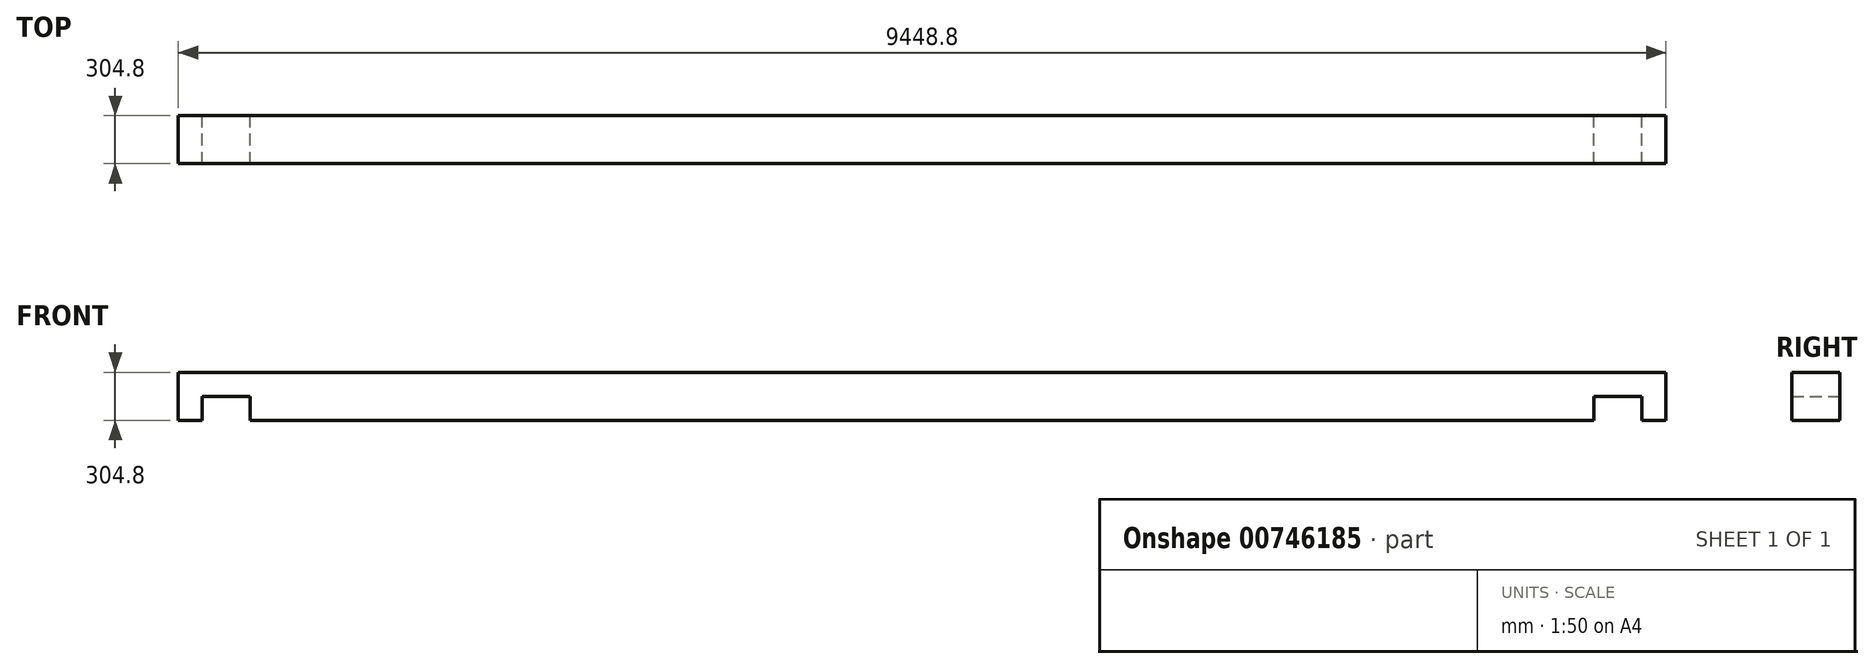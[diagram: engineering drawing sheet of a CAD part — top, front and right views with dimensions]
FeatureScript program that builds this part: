
annotation { "Feature Type Name" : "Feature", "Feature Type Description" : "" }
export const myFeature = defineFeature(function(context is Context, id is Id, definition is map)
    precondition{}
    {
        {
            var Q0;
            Q0=qCreatedBy(makeId("Front.planeOp"),FACE);
            var sketch = newSketch(context, id + "F0", { "sketchPlane" : qUnion([Q0])});
            skLineSegment(sketch, "E0", {"start": v(0, -3653.77) * mm, "end": v(0, 4269.33) * mm, "construction": true});
            skLineSegment(sketch, "E1", {"start": v(-5350.95, 0) * mm, "end": v(7707.65, 0) * mm, "construction": true});
            skLineSegment(sketch, "E2", {"start": v(0, 0) * mm, "end": v(-4267.2, 0) * mm});
            skLineSegment(sketch, "E3", {"start": v(-4267.2, 0) * mm, "end": v(-4267.2, 152.4) * mm});
            skLineSegment(sketch, "E4", {"start": v(-4267.2, 152.4) * mm, "end": v(-4572, 152.4) * mm});
            skLineSegment(sketch, "E5", {"start": v(-4572, 152.4) * mm, "end": v(-4572, 0) * mm});
            skLineSegment(sketch, "E6", {"start": v(-4572, 0) * mm, "end": v(-4724.4, 0) * mm});
            skLineSegment(sketch, "E7", {"start": v(-4724.4, 0) * mm, "end": v(-4724.4, 304.8) * mm});
            skLineSegment(sketch, "E8", {"start": v(-4724.4, 304.8) * mm, "end": v(0, 304.8) * mm});
            skLineSegment(sketch, "E9.MirrorCS", {"start": v(4267.2, 0) * mm, "end": v(4267.2, 152.4) * mm});
            skLineSegment(sketch, "E10.MirrorCS", {"start": v(4572, 0) * mm, "end": v(4724.4, 0) * mm});
            skLineSegment(sketch, "E11.MirrorCS", {"start": v(4572, 152.4) * mm, "end": v(4572, 0) * mm});
            skLineSegment(sketch, "E12.MirrorCS", {"start": v(0, 0) * mm, "end": v(4267.2, 0) * mm});
            skLineSegment(sketch, "E13.MirrorCS", {"start": v(4724.4, 0) * mm, "end": v(4724.4, 304.8) * mm});
            skLineSegment(sketch, "E14.MirrorCS", {"start": v(4724.4, 304.8) * mm, "end": v(0, 304.8) * mm});
            skLineSegment(sketch, "E15.MirrorCS", {"start": v(4267.2, 152.4) * mm, "end": v(4572, 152.4) * mm});
            skSolve(sketch);
        }
        {
            var Q0;
            Q0=makeQuery(id+"F0.imprint","IMPRINT",FACE,{"disambiguationData":[TD([[makeQuery(id+"F0.imprint","IMPRINT",EDGE,{"derivedFrom":sQuery(id+"F0.wireOp",EDGE,"E2")}),-1.0]])]});
            extrude(context, id + "F1", {"entities" : qUnion([Q0]), "depth" : 304.8 * mm, "offsetDistance" : 30.48 * mm});
        }
    });
